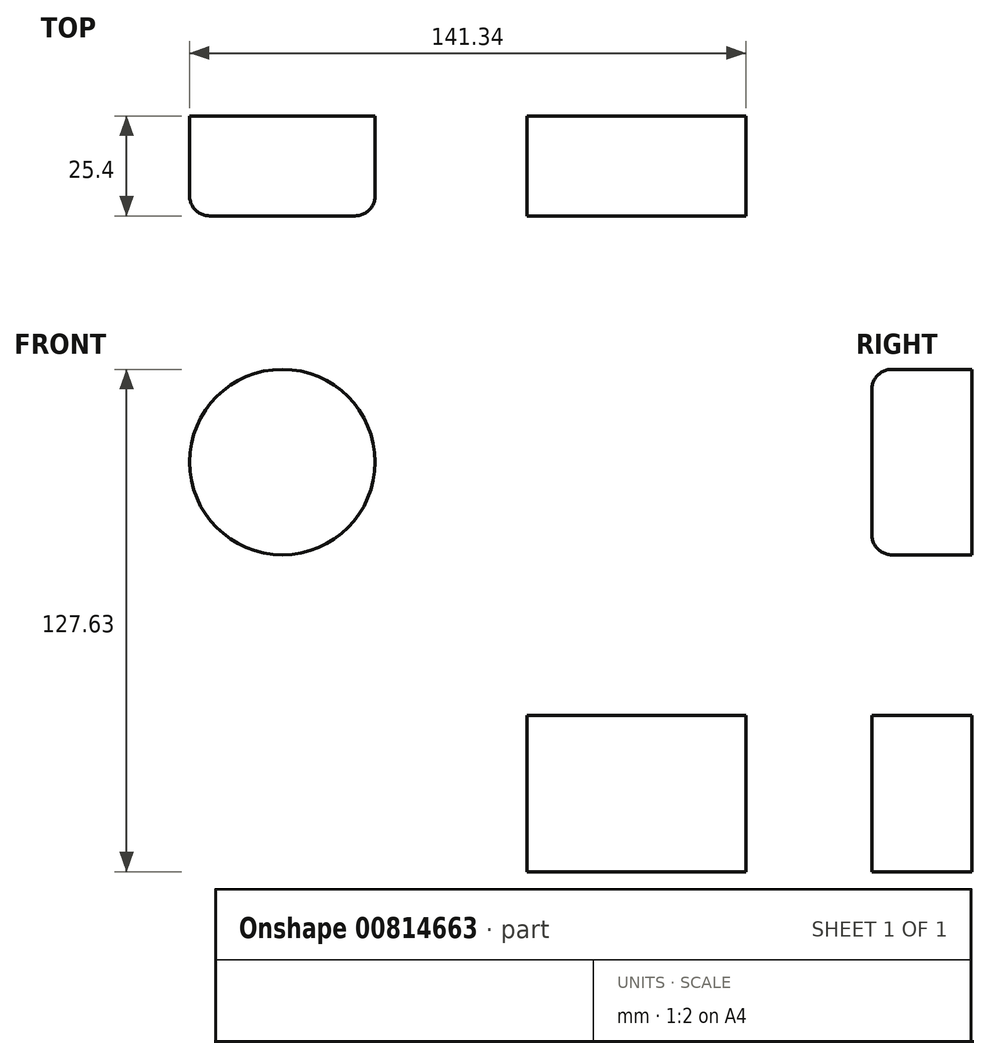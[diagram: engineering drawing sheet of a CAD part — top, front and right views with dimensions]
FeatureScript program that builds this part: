
annotation { "Feature Type Name" : "Feature", "Feature Type Description" : "" }
export const myFeature = defineFeature(function(context is Context, id is Id, definition is map)
    precondition{}
    {
        {
            var Q0;
            Q0=qCreatedBy(makeId("Front.planeOp"),FACE);
            var sketch = newSketch(context, id + "F0", { "sketchPlane" : qUnion([Q0])});
            skCircle(sketch, "E0", {"center": v(-49.38, 47.7) * mm, "radius": 23.56 * mm});
            skLineSegment(sketch, "E1.bottom", {"start": v(12.73, -16.65) * mm, "end": v(68.4, -16.65) * mm});
            skLineSegment(sketch, "E1.top", {"start": v(12.73, -56.37) * mm, "end": v(68.4, -56.37) * mm});
            skLineSegment(sketch, "E1.left", {"start": v(12.73, -16.65) * mm, "end": v(12.73, -56.37) * mm});
            skLineSegment(sketch, "E1.right", {"start": v(68.4, -16.65) * mm, "end": v(68.4, -56.37) * mm});
            skSolve(sketch);
        }
        {
            var Q0;
            Q0=makeQuery(id+"F0.imprint","IMPRINT",FACE,{"disambiguationData":[TD([[makeQuery(id+"F0.imprint","IMPRINT",EDGE,{"derivedFrom":sQuery(id+"F0.wireOp",EDGE,"E0")}),1.0]])]});
            var Q1;
            Q1=makeQuery(id+"F0.imprint","IMPRINT",FACE,{"disambiguationData":[TD([[makeQuery(id+"F0.imprint","IMPRINT",EDGE,{"derivedFrom":sQuery(id+"F0.wireOp",EDGE,"E1.bottom")}),-1.0]])]});
            extrude(context, id + "F1", {"entities" : qUnion([Q0, Q1]), "depth" : 25.4 * mm, "offsetDistance" : 25.4 * mm});
        }
        {
            var Q0;
            Q0=makeQuery(id+"F1.opExtrude","CAP_FACE",FACE,{"disambiguationData":[OSD([sQuery(id+"F0.wireOp",EDGE,"E0")])],"isStart":false});
            fillet(context, id + "F2", {"entities" : qUnion([Q0]), "radius" : 5.08 * mm, "tangentPropagation" : true, "allowEdgeOverflow" : false});
        }
    });
